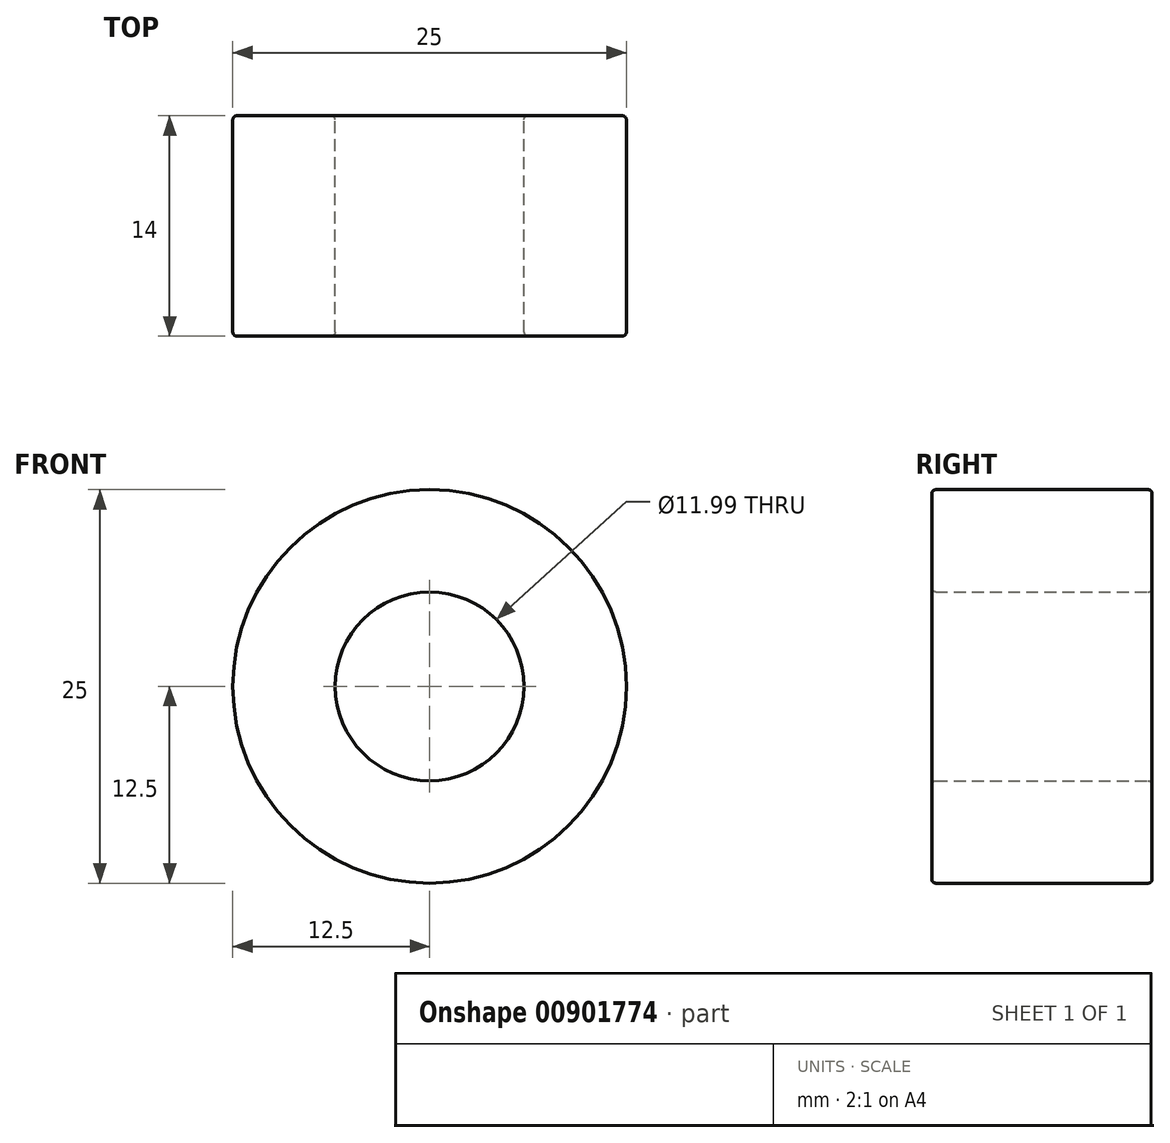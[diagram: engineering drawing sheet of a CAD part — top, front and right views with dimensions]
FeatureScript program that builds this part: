
annotation { "Feature Type Name" : "Feature", "Feature Type Description" : "" }
export const myFeature = defineFeature(function(context is Context, id is Id, definition is map)
    precondition{}
    {
        {
            var Q0;
            Q0=qCreatedBy(makeId("Front.planeOp"),FACE);
            var sketch = newSketch(context, id + "F0", { "sketchPlane" : qUnion([Q0])});
            skCircle(sketch, "E0", {"center": v(0, 0) * mm, "radius": 6 * mm});
            skCircle(sketch, "E1", {"center": v(0, 0) * mm, "radius": 12.5 * mm});
            skSolve(sketch);
        }
        {
            var Q0;
            Q0=makeQuery(id+"F0.imprint","IMPRINT",FACE,{"disambiguationData":[TD([[makeQuery(id+"F0.imprint","IMPRINT",EDGE,{"derivedFrom":sQuery(id+"F0.wireOp",EDGE,"E0")}),-1.0]])]});
            extrude(context, id + "F1", {"entities" : qUnion([Q0]), "depth" : 14 * mm, "offsetDistance" : 25 * mm});
        }
        {
            var Q0;
            Q0=makeQuery(id+"F1.opExtrude","CAP_EDGE",EDGE,{"disambiguationData":[OSD([sQuery(id+"F0.wireOp",EDGE,"E1")])],"isStart":false});
            var Q1;
            Q1=makeQuery(id+"F1.opExtrude","CAP_EDGE",EDGE,{"disambiguationData":[OSD([sQuery(id+"F0.wireOp",EDGE,"E0")])],"isStart":false});
            var Q2;
            Q2=makeQuery(id+"F1.opExtrude","SWEPT_FACE",FACE,{"disambiguationData":[OSD([sQuery(id+"F0.wireOp",EDGE,"E0")])]});
            var Q3;
            Q3=makeQuery(id+"F1.opExtrude","CAP_EDGE",EDGE,{"disambiguationData":[OSD([sQuery(id+"F0.wireOp",EDGE,"E1")])],"isStart":true});
            fillet(context, id + "F2", {"entities" : qUnion([Q0, Q1, Q2, Q3]), "radius" : 0.25 * mm, "tangentPropagation" : true, "allowEdgeOverflow" : false});
        }
    });
